# Revit family: NLRS_57_AIR_UN_wall-grill-wuaa-supply-LT_sacs
name_source: partatom
category: Air Terminals
units: mm (PartAtom-declared; Revit-internal decimal feet)

## family parameters
Always vertical = No
Cut with Voids When Loaded = Yes
OmniClass Number = 23.75.70.21.27.11
OmniClass Title = Diffusers, Registers, and Grilles
Part Type = Normal
Room Calculation Point = Yes
Round Connector Dimension = Use Diameter
Shared = No
Work Plane-Based = No

## types (2) — shared parameters
Assembly Code = 57.0
Description = Solid Air wall diffuser WUAA (supply)
FactorTable = WUAA_Factors (supply)
FireRating = 0
IfcDescription = Solid Air wall diffuser WUAA (supply)
IfcExportAs = IfcAirTerminal
IfcExportType = DIFFUSER
IsExternal = No
LoadBearing = No
LookupTable = WUAA
Manufacturer = Solid Air Climate Systems
Max Flow = 0.0 m³/h
Min Flow = 0.0 m³/h
Model = Wall diffuser
NLRS_C_content_datum_uitgifte = 08-08-2022
NLRS_C_content_provider = Solid Air Climate Solutions
NLRS_C_content_versie = 3.19.02
NLRS_C_niveau ontwikkeling = LOD 400
SACS_Material_Frame = Extruded Aluminium
SACS_Material_VCD = Extruded Aluminium
SACS_Show_Symbol = No

## per-type parameters (varying)
| type | SACS_Base_Index | URL |
| WUAAO | 1 | https://solid-air.com |
| WUAAV | 2 | https://solid-air.nl |

## geometry (parser evidence)
native form markers: Sweep x14
no freeform markers — native parametric forms only
